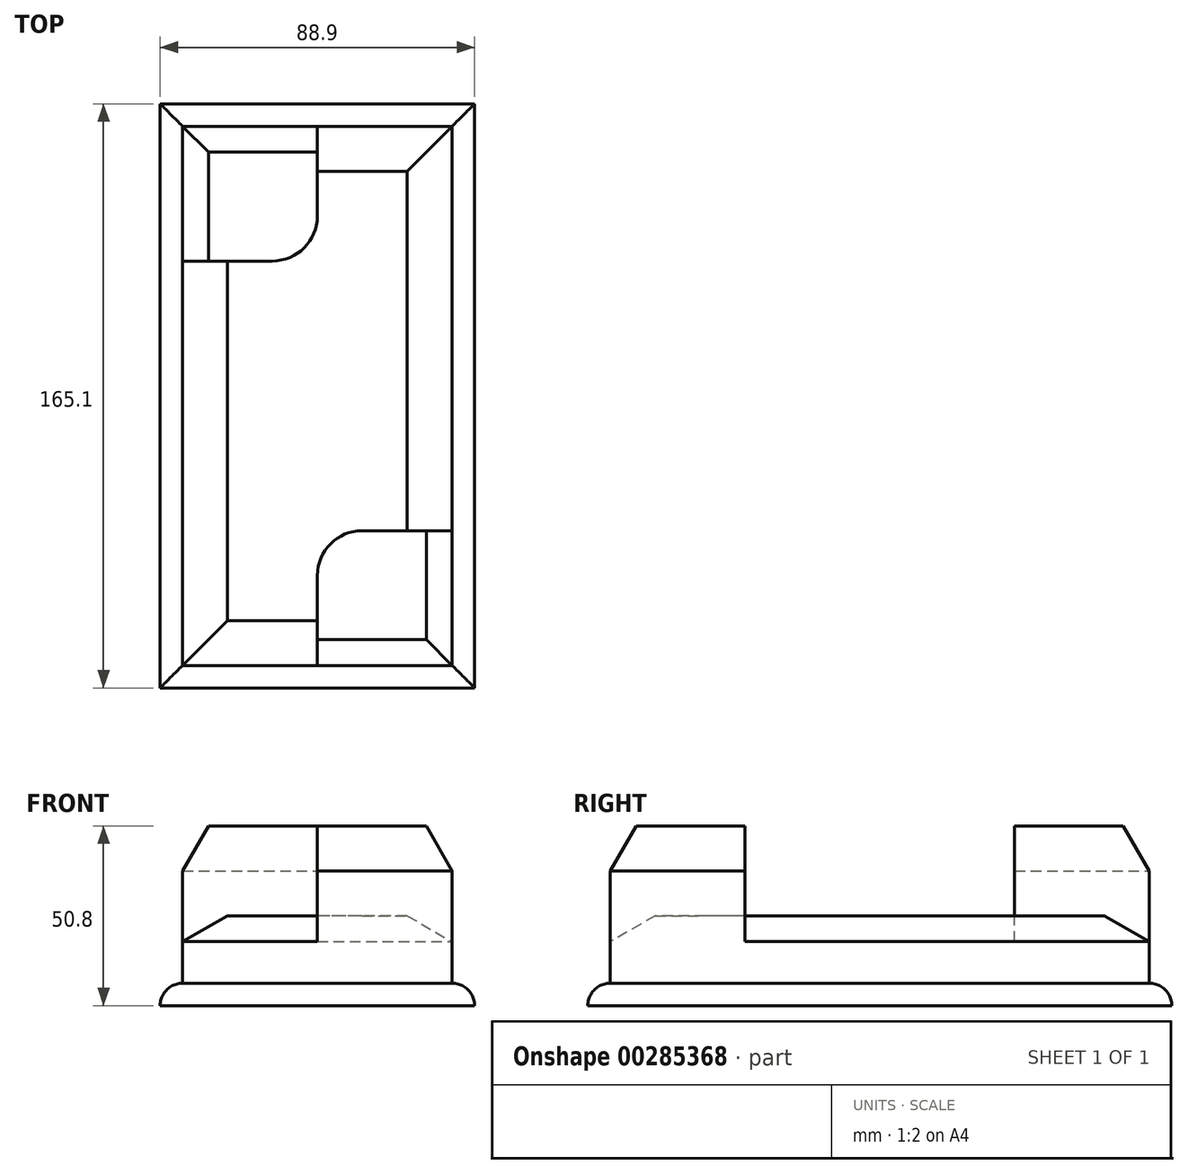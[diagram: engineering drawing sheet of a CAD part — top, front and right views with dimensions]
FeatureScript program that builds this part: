
annotation { "Feature Type Name" : "Feature", "Feature Type Description" : "" }
export const myFeature = defineFeature(function(context is Context, id is Id, definition is map)
    precondition{}
    {
        {
            var Q0;
            Q0=qCreatedBy(makeId("Top.planeOp"),FACE);
            var sketch = newSketch(context, id + "F0", { "sketchPlane" : qUnion([Q0])});
            skLineSegment(sketch, "E0.bottom", {"start": v(-38.1, 76.2) * mm, "end": v(38.1, 76.2) * mm});
            skLineSegment(sketch, "E0.top", {"start": v(-38.1, -76.2) * mm, "end": v(38.1, -76.2) * mm});
            skLineSegment(sketch, "E0.left", {"start": v(-38.1, 76.2) * mm, "end": v(-38.1, -76.2) * mm});
            skLineSegment(sketch, "E0.right", {"start": v(38.1, 76.2) * mm, "end": v(38.1, -76.2) * mm});
            skPoint(sketch, "E0.middle", {"position": v(0, 0) * mm});
            skLineSegment(sketch, "E1.bottom", {"start": v(-44.45, 82.55) * mm, "end": v(44.45, 82.55) * mm});
            skLineSegment(sketch, "E1.top", {"start": v(-44.45, -82.55) * mm, "end": v(44.45, -82.55) * mm});
            skLineSegment(sketch, "E1.left", {"start": v(-44.45, 82.55) * mm, "end": v(-44.45, -82.55) * mm});
            skLineSegment(sketch, "E1.right", {"start": v(44.45, 82.55) * mm, "end": v(44.45, -82.55) * mm});
            skPoint(sketch, "E2.endSnap0", {"position": v(0, 76.2) * mm});
            skPoint(sketch, "E3.endSnap0", {"position": v(0, -76.2) * mm});
            skLineSegment(sketch, "E4", {"start": v(0, 76.2) * mm, "end": v(0, 50.8) * mm});
            skLineSegment(sketch, "E5", {"start": v(-12.7, 38.1) * mm, "end": v(-38.1, 38.1) * mm});
            skLineSegment(sketch, "E6", {"start": v(0, -76.2) * mm, "end": v(0, -50.8) * mm});
            skLineSegment(sketch, "E7", {"start": v(12.7, -38.1) * mm, "end": v(38.1, -38.1) * mm});
            skPoint(sketch, "E8.visualSharp", {"position": v(0, 38.1) * mm});
            skArc(sketch, "E8.filletArc", {"start": v(-12.7, 38.1) * mm, "mid": v(-3.72, 41.82) * mm, "end": v(0, 50.8) * mm});
            skPoint(sketch, "E9.visualSharp", {"position": v(0, -38.1) * mm});
            skArc(sketch, "E9.filletArc", {"start": v(12.7, -38.1) * mm, "mid": v(3.72, -41.82) * mm, "end": v(0, -50.8) * mm});
            skSolve(sketch);
        }
        {
            var Q0;
            Q0 = qSketchRegion(id + "F0", true);
            extrude(context, id + "F1", {"entities" : qUnion([Q0]), "depth" : 6.35 * mm});
        }
        {
            var Q0;
            {var subQ9=sQuery(id+"F0.wireOp",EDGE,"E4");Q0=makeQuery(id+"F0.imprint","IMPRINT",FACE,{"disambiguationData":[TD([[makeQuery(id+"F0.imprint","IMPRINT",EDGE,{"derivedFrom":subQ9}),1.0]])]});}
            extrude(context, id + "F2", {"entities" : qUnion([Q0]), "operationType" : NewBodyOperationType.ADD, "depth" : 25.4 * mm});
        }
        {
            var Q0;
            {var subQ1=sQuery(id+"F0.wireOp",EDGE,"E4");Q0=makeQuery(id+"F0.imprint","IMPRINT",FACE,{"disambiguationData":[TD([[makeQuery(id+"F0.imprint","IMPRINT",EDGE,{"derivedFrom":subQ1}),-1.0]])]});}
            var Q1;
            {var subQ4=sQuery(id+"F0.wireOp",EDGE,"E6");Q1=makeQuery(id+"F0.imprint","IMPRINT",FACE,{"disambiguationData":[TD([[makeQuery(id+"F0.imprint","IMPRINT",EDGE,{"derivedFrom":subQ4}),-1.0]])]});}
            extrude(context, id + "F3", {"entities" : qUnion([Q0, Q1]), "operationType" : NewBodyOperationType.ADD, "depth" : 50.8 * mm});
        }
        {
            var Q0;
            Q0=makeQuery(id+"F2.opExtrude","CAP_EDGE",EDGE,{"disambiguationData":[OSD([sQuery(id+"F0.wireOp",EDGE,"E0.left")])],"isStart":false});
            var Q1;
            Q1=makeQuery(id+"F2.opExtrude","CAP_EDGE",EDGE,{"disambiguationData":[OSD([sQuery(id+"F0.wireOp",EDGE,"E0.top")])],"isStart":false});
            var Q2;
            Q2=makeQuery(id+"F2.opExtrude","CAP_EDGE",EDGE,{"disambiguationData":[OSD([sQuery(id+"F0.wireOp",EDGE,"E0.right")])],"isStart":false});
            var Q3;
            Q3=makeQuery(id+"F2.opExtrude","CAP_EDGE",EDGE,{"disambiguationData":[OSD([sQuery(id+"F0.wireOp",EDGE,"E0.bottom")])],"isStart":false});
            chamfer(context, id + "F4", {"entities" : qUnion([Q0, Q1, Q2, Q3]), "chamferType" : ChamferType.OFFSET_ANGLE, "width" : 12.7 * mm, "oppositeDirection" : false, "angle" : 30 * degree, "tangentPropagation" : true});
        }
        {
            var Q0;
            Q0=makeQuery(id+"F1.opExtrude","CAP_EDGE",EDGE,{"disambiguationData":[OSD([sQuery(id+"F0.wireOp",EDGE,"E1.right")])],"isStart":false});
            var Q1;
            Q1=makeQuery(id+"F1.opExtrude","CAP_EDGE",EDGE,{"disambiguationData":[OSD([sQuery(id+"F0.wireOp",EDGE,"E1.top")])],"isStart":false});
            var Q2;
            Q2=makeQuery(id+"F1.opExtrude","CAP_EDGE",EDGE,{"disambiguationData":[OSD([sQuery(id+"F0.wireOp",EDGE,"E1.left")])],"isStart":false});
            var Q3;
            Q3=makeQuery(id+"F1.opExtrude","CAP_EDGE",EDGE,{"disambiguationData":[OSD([sQuery(id+"F0.wireOp",EDGE,"E1.bottom")])],"isStart":false});
            fillet(context, id + "F5", {"entities" : qUnion([Q0, Q1, Q2, Q3]), "radius" : 6.35 * mm, "tangentPropagation" : true, "allowEdgeOverflow" : false});
        }
        {
            var Q0;
            Q0=makeQuery(id+"F3.opExtrude","CAP_EDGE",EDGE,{"disambiguationData":[OSD([sQuery(id+"F0.wireOp",EDGE,"E0.bottom")])],"isStart":false});
            var Q1;
            Q1=makeQuery(id+"F3.opExtrude","CAP_EDGE",EDGE,{"disambiguationData":[OSD([sQuery(id+"F0.wireOp",EDGE,"E0.left")])],"isStart":false});
            chamfer(context, id + "F6", {"entities" : qUnion([Q0, Q1]), "chamferType" : ChamferType.OFFSET_ANGLE, "width" : 12.7 * mm, "oppositeDirection" : false, "angle" : 30 * degree, "tangentPropagation" : true});
        }
        {
            var Q0;
            Q0=makeQuery(id+"F3.opExtrude","CAP_EDGE",EDGE,{"disambiguationData":[OSD([sQuery(id+"F0.wireOp",EDGE,"E0.right")])],"isStart":false});
            var Q1;
            Q1=makeQuery(id+"F3.opExtrude","CAP_EDGE",EDGE,{"disambiguationData":[OSD([sQuery(id+"F0.wireOp",EDGE,"E0.top")])],"isStart":false});
            chamfer(context, id + "F7", {"entities" : qUnion([Q0, Q1]), "chamferType" : ChamferType.OFFSET_ANGLE, "width" : 12.7 * mm, "oppositeDirection" : false, "angle" : 30 * degree, "tangentPropagation" : true});
        }
    });
